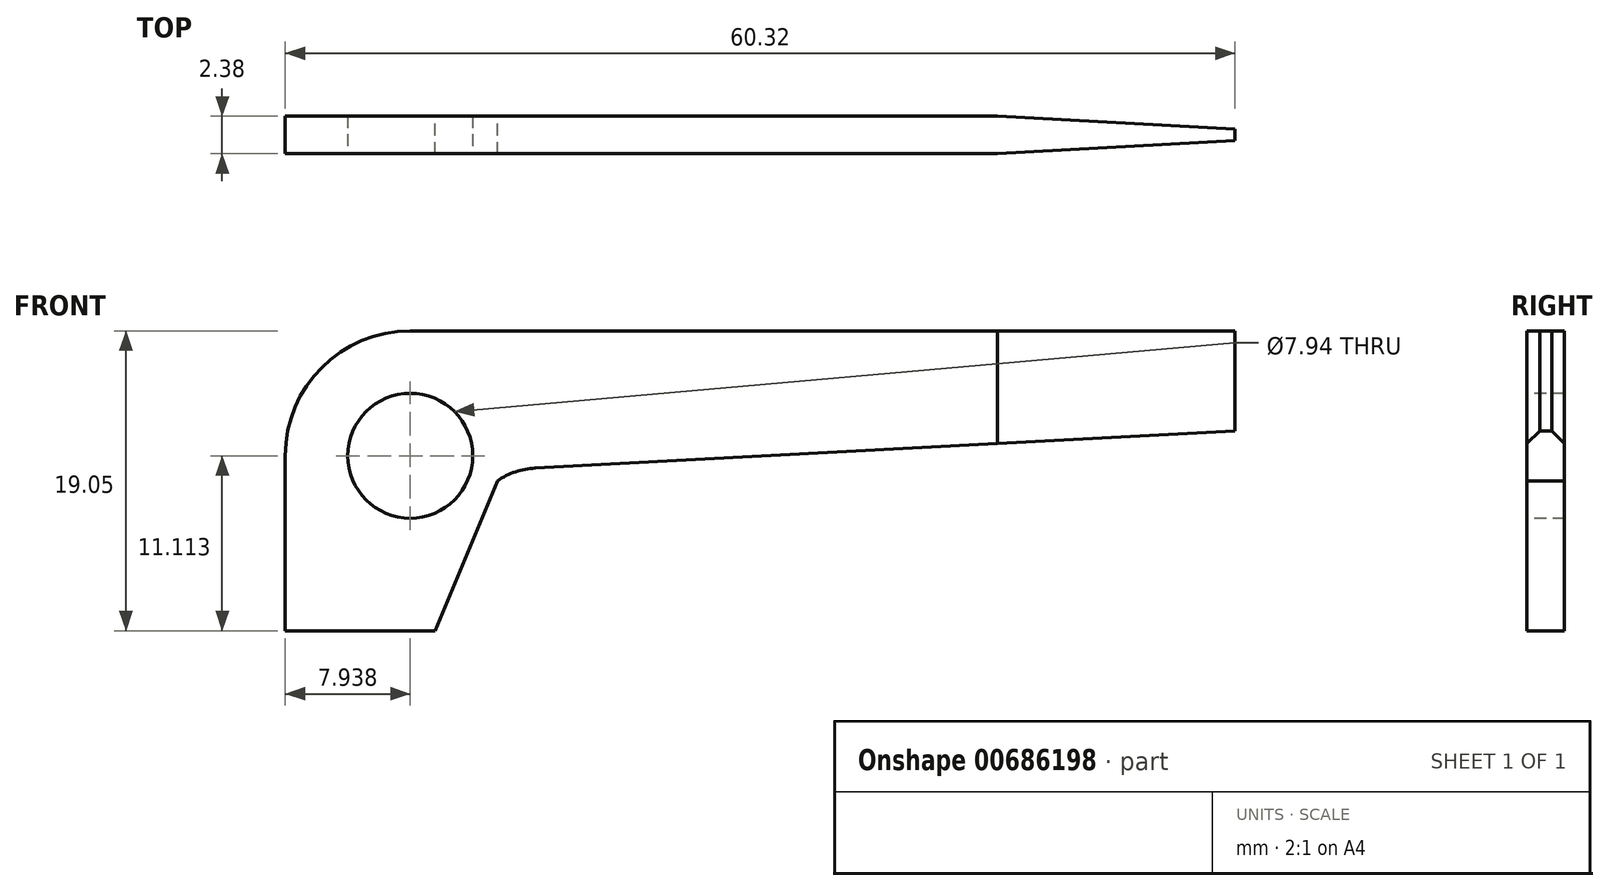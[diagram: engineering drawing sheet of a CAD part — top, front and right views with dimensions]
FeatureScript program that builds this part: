
annotation { "Feature Type Name" : "Feature", "Feature Type Description" : "" }
export const myFeature = defineFeature(function(context is Context, id is Id, definition is map)
    precondition{}
    {
        {
            var Q0;
            Q0=qCreatedBy(makeId("Front.planeOp"),FACE);
            var sketch = newSketch(context, id + "F0", { "sketchPlane" : qUnion([Q0])});
            skLineSegment(sketch, "E0.top", {"start": v(7.94, 19.05) * mm, "end": v(60.32, 19.05) * mm});
            skLineSegment(sketch, "E0.left", {"start": v(0, 0) * mm, "end": v(0, 11.11) * mm});
            skLineSegment(sketch, "E1", {"start": v(13.48, 9.53) * mm, "end": v(9.53, 0) * mm});
            skPoint(sketch, "E1.startSnap0", {"position": v(0, 9.53) * mm});
            skLineSegment(sketch, "E2", {"start": v(9.53, 0) * mm, "end": v(13.48, 9.53) * mm});
            skLineSegment(sketch, "E3", {"start": v(60.33, 12.7) * mm, "end": v(15.87, 10.33) * mm});
            skLineSegment(sketch, "E4", {"start": v(0, 0) * mm, "end": v(9.53, 0) * mm});
            skLineSegment(sketch, "E5", {"start": v(60.33, 19.05) * mm, "end": v(60.33, 12.7) * mm});
            skArc(sketch, "E6", {"start": v(15.87, 10.33) * mm, "mid": v(14.62, 10.1) * mm, "end": v(13.48, 9.53) * mm});
            skPoint(sketch, "E7.visualSharp", {"position": v(0, 19.05) * mm});
            skArc(sketch, "E7.filletArc", {"start": v(7.94, 19.05) * mm, "mid": v(2.32, 16.73) * mm, "end": v(0, 11.11) * mm});
            skSolve(sketch);
        }
        {
            var Q0;
            Q0 = qSketchRegion(id + "F0", true);
            extrude(context, id + "F1", {"entities" : qUnion([Q0]), "depth" : 2.38 * mm, "offsetDistance" : 25.4 * mm});
        }
        {
            var Q0;
            Q0=makeQuery(id+"F1.opExtrude","CAP_FACE",FACE,{"disambiguationData":[OSD([sQuery(id+"F0.wireOp",EDGE,"E0.top"),sQuery(id+"F0.wireOp",EDGE,"E0.left"),sQuery(id+"F0.wireOp",EDGE,"E2"),sQuery(id+"F0.wireOp",EDGE,"E3"),sQuery(id+"F0.wireOp",EDGE,"E4"),sQuery(id+"F0.wireOp",EDGE,"E5"),sQuery(id+"F0.wireOp",EDGE,"E6"),sQuery(id+"F0.wireOp",EDGE,"E7.filletArc")])],"isStart":false});
            var sketch = newSketch(context, id + "F2", { "sketchPlane" : qUnion([Q0])});
            skCircle(sketch, "E8", {"center": v(7.94, 11.11) * mm, "radius": 3.97 * mm});
            skSolve(sketch);
        }
        {
            var Q0;
            Q0=makeQuery(id+"F2.imprint","IMPRINT",FACE,{"disambiguationData":[TD([[makeQuery(id+"F2.imprint","IMPRINT",EDGE,{"derivedFrom":sQuery(id+"F2.wireOp",EDGE,"E8")}),1.0]])]});
            var sketch = newSketch(context, id + "F3", { "sketchPlane" : qUnion([Q0])});
            skSolve(sketch);
        }
        {
            var Q0;
            Q0=makeQuery(id+"F3.imprint","IMPRINT",FACE,{"disambiguationData":[TD([[makeQuery(id+"F3.imprint","IMPRINT",EDGE,{"derivedFrom":makeQuery(id+"F2.imprint","IMPRINT",EDGE,{"derivedFrom":sQuery(id+"F2.wireOp",EDGE,"E8")})}),1.0]])]});
            var sketch = newSketch(context, id + "F4", { "sketchPlane" : qUnion([Q0])});
            skSolve(sketch);
        }
        {
            var Q0;
            Q0=makeQuery(id+"F4.imprint","IMPRINT",FACE,{"disambiguationData":[TD([[makeQuery(id+"F4.imprint","IMPRINT",EDGE,{"derivedFrom":makeQuery(id+"F3.imprint","IMPRINT",EDGE,{"derivedFrom":makeQuery(id+"F2.imprint","IMPRINT",EDGE,{"derivedFrom":sQuery(id+"F2.wireOp",EDGE,"E8")})})}),1.0]])]});
            extrude(context, id + "F5", {"entities" : qUnion([Q0]), "operationType" : NewBodyOperationType.REMOVE, "oppositeDirection" : true, "depth" : 25.4 * mm, "offsetDistance" : 25.4 * mm});
        }
        {
            var Q0;
            Q0=makeQuery(id+"F1.opExtrude","SWEPT_FACE",FACE,{"disambiguationData":[OSD([sQuery(id+"F0.wireOp",EDGE,"E0.top")])]});
            var sketch = newSketch(context, id + "F6", { "sketchPlane" : qUnion([Q0])});
            skLineSegment(sketch, "E9", {"start": v(45.24, 0) * mm, "end": v(60.32, -0.82) * mm});
            skLineSegment(sketch, "E10", {"start": v(60.32, -0.82) * mm, "end": v(60.32, 0) * mm});
            skLineSegment(sketch, "E11", {"start": v(60.32, 0) * mm, "end": v(45.24, 0) * mm});
            skLineSegment(sketch, "E12.MirrorCS", {"start": v(45.24, -2.38) * mm, "end": v(60.32, -1.56) * mm});
            skLineSegment(sketch, "E13.MirrorCS", {"start": v(60.32, -2.38) * mm, "end": v(45.24, -2.38) * mm});
            skLineSegment(sketch, "E14.MirrorCS", {"start": v(60.32, -1.56) * mm, "end": v(60.32, -2.38) * mm});
            skSolve(sketch);
        }
        {
            var Q0;
            Q0=makeQuery(id+"F6.imprint","IMPRINT",FACE,{"disambiguationData":[TD([[makeQuery(id+"F6.imprint","IMPRINT",EDGE,{"derivedFrom":sQuery(id+"F6.wireOp",EDGE,"E9")}),1.0]])]});
            var Q1;
            Q1=makeQuery(id+"F6.imprint","IMPRINT",FACE,{"disambiguationData":[TD([[makeQuery(id+"F6.imprint","IMPRINT",EDGE,{"derivedFrom":sQuery(id+"F6.wireOp",EDGE,"E12.MirrorCS")}),-1.0]])]});
            extrude(context, id + "F7", {"entities" : qUnion([Q0, Q1]), "operationType" : NewBodyOperationType.REMOVE, "oppositeDirection" : true, "depth" : 25.4 * mm, "offsetDistance" : 25.4 * mm});
        }
    });
